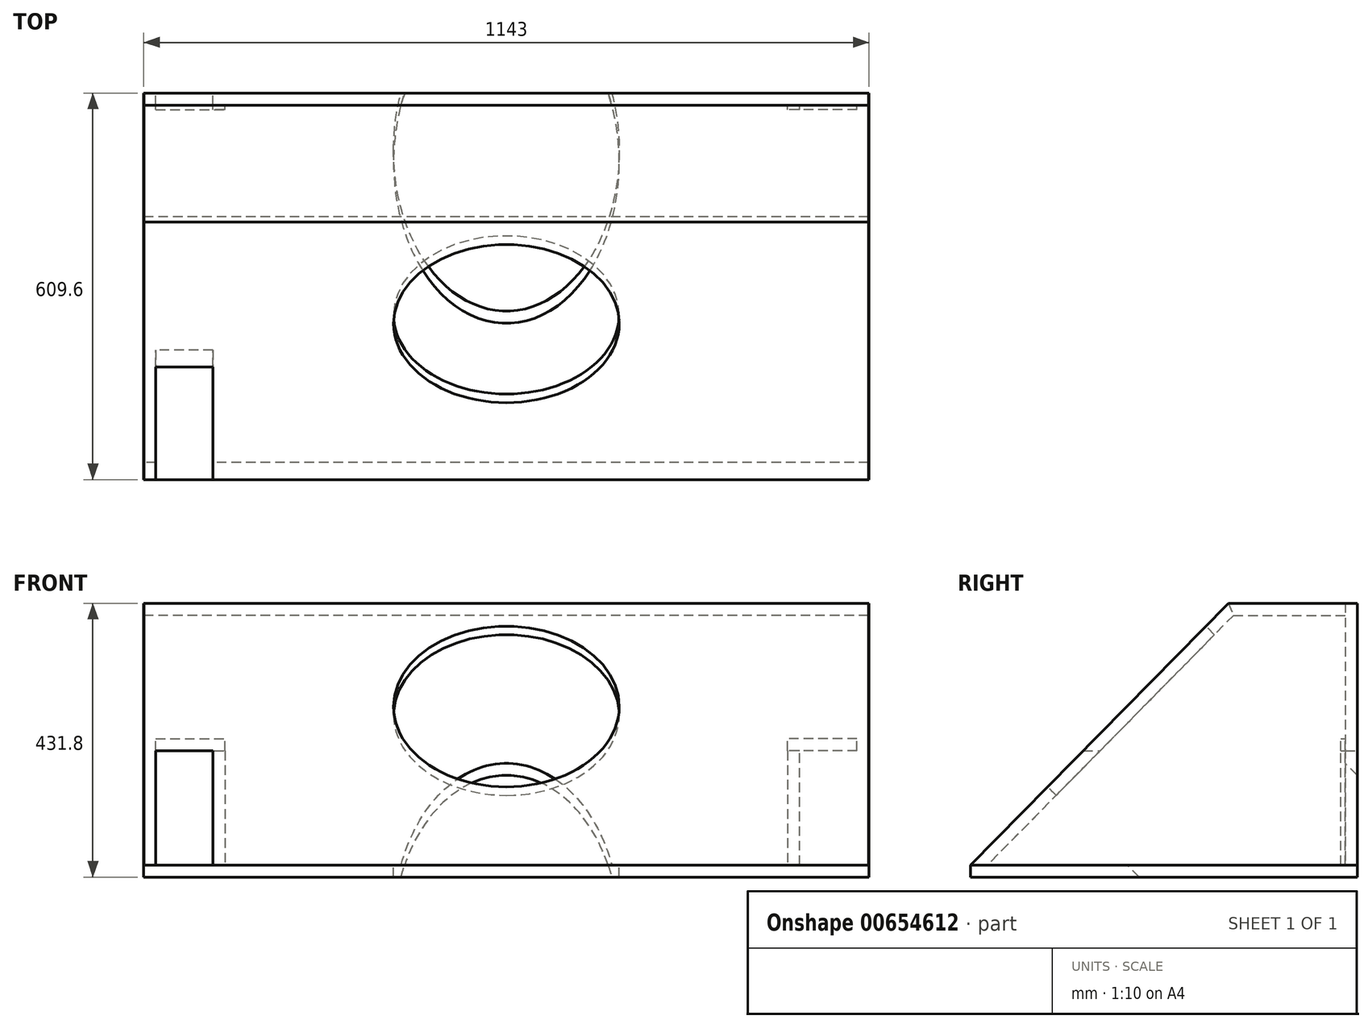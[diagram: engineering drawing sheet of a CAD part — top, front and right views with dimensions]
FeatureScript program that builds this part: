
annotation { "Feature Type Name" : "Feature", "Feature Type Description" : "" }
export const myFeature = defineFeature(function(context is Context, id is Id, definition is map)
    precondition{}
    {
        {
            assignVariable(context, id + "F0", {"name" : "Thickness", "anyValue" : 0.75});
        }
        {
            var Q0;
            Q0=qCreatedBy(makeId("Top.planeOp"),FACE);
            var sketch = newSketch(context, id + "F1", { "sketchPlane" : qUnion([Q0])});
            skLineSegment(sketch, "E0.bottom", {"start": v(571.5, 304.8) * mm, "end": v(-571.5, 304.8) * mm});
            skLineSegment(sketch, "E0.top", {"start": v(571.5, -304.8) * mm, "end": v(-571.5, -304.8) * mm});
            skLineSegment(sketch, "E0.left", {"start": v(571.5, 304.8) * mm, "end": v(571.5, -304.8) * mm});
            skLineSegment(sketch, "E0.right", {"start": v(-571.5, 304.8) * mm, "end": v(-571.5, -304.8) * mm});
            skPoint(sketch, "E0.middle", {"position": v(0, 0) * mm});
            skSolve(sketch);
        }
        {
            var Q0;
            Q0=qCreatedBy(makeId("Right.planeOp"),FACE);
            var Q1;
            Q1=sQuery(id+"F1.wireOp",VERTEX,"E0.left.end");
            cPlane(context, id + "F2", {"entities" : qUnion([Q0, Q1]), "cplaneType" : CPlaneType.PLANE_POINT, "offset" : 25.4 * mm, "width" : 152.4 * mm, "height" : 152.4 * mm});
        }
        {
            var Q0;
            Q0=qCreatedBy(id+"F2.planeOp",FACE);
            var sketch = newSketch(context, id + "F3", { "sketchPlane" : qUnion([Q0])});
            skLineSegment(sketch, "E1", {"start": v(-304.8, 0) * mm, "end": v(101.6, 412.75) * mm});
            skLineSegment(sketch, "E2", {"start": v(101.6, 412.75) * mm, "end": v(304.8, 412.75) * mm});
            skLineSegment(sketch, "E3", {"start": v(304.8, 412.75) * mm, "end": v(304.8, 0) * mm});
            skLineSegment(sketch, "E4", {"start": v(-304.8, 0) * mm, "end": v(304.8, 0) * mm});
            skSolve(sketch);
        }
        {
            var Q0;
            Q0=makeQuery(id+"F3.imprint","IMPRINT",FACE,{"disambiguationData":[TD([[makeQuery(id+"F3.imprint","IMPRINT",EDGE,{"derivedFrom":sQuery(id+"F3.wireOp",EDGE,"E1")}),-1.0]])]});
            extrude(context, id + "F4", {"entities" : qUnion([Q0]), "oppositeDirection" : true, "depth" : (getVariable(context, 'Thickness')) * mm, "offsetDistance" : 25.4 * mm});
        }
        {
            var Q0;
            Q0=qCreatedBy(id+"F2.planeOp",FACE);
            var sketch = newSketch(context, id + "F5", { "sketchPlane" : qUnion([Q0])});
            skLineSegment(sketch, "E5", {"start": v(304.8, 0) * mm, "end": v(-304.8, 0) * mm});
            skLineSegment(sketch, "E6", {"start": v(-304.8, -19.05) * mm, "end": v(-304.8, 0) * mm});
            skLineSegment(sketch, "E7", {"start": v(-304.8, -19.05) * mm, "end": v(304.8, -19.05) * mm});
            skLineSegment(sketch, "E8", {"start": v(304.8, -19.05) * mm, "end": v(304.8, 0) * mm});
            skSolve(sketch);
        }
        {
            var Q0;
            Q0=makeQuery(id+"F4.opExtrude","SWEPT_BODY",BODY,{"disambiguationData":[OSD([sQuery(id+"F3.wireOp",EDGE,"E1"),sQuery(id+"F3.wireOp",EDGE,"E2"),sQuery(id+"F3.wireOp",EDGE,"E3"),sQuery(id+"F3.wireOp",EDGE,"E4")])]});
            var Q1;
            Q1=qCreatedBy(makeId("Right.planeOp"),FACE);
            mirror(context, id + "F6", {"entities" : qUnion([Q0]), "mirrorPlane" : qUnion([Q1])});
        }
        {
            var Q0;
            Q0 = qSketchRegion(id + "F5", true);
            var Q1;
            Q1=makeQuery(id+"F6.opPattern","COPY",FACE,{"derivedFrom":makeQuery(id+"F4.opExtrude","CAP_FACE",FACE,{"disambiguationData":[OSD([sQuery(id+"F3.wireOp",EDGE,"E1"),sQuery(id+"F3.wireOp",EDGE,"E2"),sQuery(id+"F3.wireOp",EDGE,"E3"),sQuery(id+"F3.wireOp",EDGE,"E4")])],"isStart":true}),"instanceName":"1"});
            var Q2;
            Q2=makeQuery(id+"F6.opPattern","COPY",FACE,{"derivedFrom":makeQuery(id+"F4.opExtrude","CAP_FACE",FACE,{"disambiguationData":[OSD([sQuery(id+"F3.wireOp",EDGE,"E1"),sQuery(id+"F3.wireOp",EDGE,"E2"),sQuery(id+"F3.wireOp",EDGE,"E3"),sQuery(id+"F3.wireOp",EDGE,"E4")])],"isStart":false}),"instanceName":"1"});
            extrude(context, id + "F7", {"entities" : qUnion([Q0]), "endBound" : BoundingType.UP_TO_SURFACE, "oppositeDirection" : true, "depth" : 25.4 * mm, "endBoundEntityFace" : qUnion([Q1]), "offsetDistance" : 25.4 * mm});
        }
        {
            var Q0;
            Q0=qCreatedBy(makeId("Right.planeOp"),FACE);
            var sketch = newSketch(context, id + "F8", { "sketchPlane" : qUnion([Q0])});
            skLineSegment(sketch, "E9", {"start": v(-304.8, 0) * mm, "end": v(-278.07, 0) * mm});
            skLineSegment(sketch, "E10", {"start": v(-278.07, 0) * mm, "end": v(109.58, 393.7) * mm});
            skLineSegment(sketch, "E11", {"start": v(109.58, 393.7) * mm, "end": v(101.6, 412.75) * mm});
            skLineSegment(sketch, "E12", {"start": v(101.6, 412.75) * mm, "end": v(-304.8, 0) * mm});
            skSolve(sketch);
        }
        {
            var Q0;
            Q0 = qSketchRegion(id + "F8", true);
            var Q1;
            Q1=makeQuery(id+"F4.opExtrude","CAP_FACE",FACE,{"disambiguationData":[OSD([sQuery(id+"F3.wireOp",EDGE,"E1"),sQuery(id+"F3.wireOp",EDGE,"E2"),sQuery(id+"F3.wireOp",EDGE,"E3"),sQuery(id+"F3.wireOp",EDGE,"E4")])],"isStart":false});
            var Q2;
            Q2=makeQuery(id+"F6.opPattern","COPY",FACE,{"derivedFrom":makeQuery(id+"F4.opExtrude","CAP_FACE",FACE,{"disambiguationData":[OSD([sQuery(id+"F3.wireOp",EDGE,"E1"),sQuery(id+"F3.wireOp",EDGE,"E2"),sQuery(id+"F3.wireOp",EDGE,"E3"),sQuery(id+"F3.wireOp",EDGE,"E4")])],"isStart":false}),"instanceName":"1"});
            extrude(context, id + "F9", {"entities" : qUnion([Q0]), "endBound" : BoundingType.UP_TO_SURFACE, "depth" : 25.4 * mm, "endBoundEntityFace" : qUnion([Q1]), "offsetDistance" : 25.4 * mm, "hasSecondDirection" : true, "secondDirectionBound" : SecondDirectionBoundingType.UP_TO_SURFACE, "secondDirectionOppositeDirection" : true, "secondDirectionDepth" : 25.4 * mm, "secondDirectionBoundEntityFace" : qUnion([Q2])});
        }
        {
            var Q0;
            Q0=qCreatedBy(makeId("Right.planeOp"),FACE);
            var sketch = newSketch(context, id + "F10", { "sketchPlane" : qUnion([Q0])});
            skLineSegment(sketch, "E13", {"start": v(285.75, 412.75) * mm, "end": v(285.75, 0) * mm});
            skLineSegment(sketch, "E14", {"start": v(285.75, 412.75) * mm, "end": v(304.8, 412.75) * mm});
            skLineSegment(sketch, "E15", {"start": v(304.8, 0) * mm, "end": v(304.8, 412.75) * mm});
            skLineSegment(sketch, "E16", {"start": v(304.8, 0) * mm, "end": v(285.75, 0) * mm});
            skSolve(sketch);
        }
        {
            var Q0;
            Q0 = qSketchRegion(id + "F10", true);
            var Q1;
            Q1=makeQuery(id+"F4.opExtrude","CAP_FACE",FACE,{"disambiguationData":[OSD([sQuery(id+"F3.wireOp",EDGE,"E1"),sQuery(id+"F3.wireOp",EDGE,"E2"),sQuery(id+"F3.wireOp",EDGE,"E3"),sQuery(id+"F3.wireOp",EDGE,"E4")])],"isStart":false});
            var Q2;
            Q2=makeQuery(id+"F6.opPattern","COPY",FACE,{"derivedFrom":makeQuery(id+"F4.opExtrude","CAP_FACE",FACE,{"disambiguationData":[OSD([sQuery(id+"F3.wireOp",EDGE,"E1"),sQuery(id+"F3.wireOp",EDGE,"E2"),sQuery(id+"F3.wireOp",EDGE,"E3"),sQuery(id+"F3.wireOp",EDGE,"E4")])],"isStart":false}),"instanceName":"1"});
            extrude(context, id + "F11", {"entities" : qUnion([Q0]), "endBound" : BoundingType.UP_TO_SURFACE, "depth" : 25.4 * mm, "endBoundEntityFace" : qUnion([Q1]), "offsetDistance" : 25.4 * mm, "hasSecondDirection" : true, "secondDirectionBound" : SecondDirectionBoundingType.UP_TO_SURFACE, "secondDirectionOppositeDirection" : true, "secondDirectionDepth" : 25.4 * mm, "secondDirectionBoundEntityFace" : qUnion([Q2])});
        }
        {
            var Q0;
            Q0=makeQuery(id+"F6.opPattern","COPY",FACE,{"derivedFrom":makeQuery(id+"F4.opExtrude","CAP_FACE",FACE,{"disambiguationData":[OSD([sQuery(id+"F3.wireOp",EDGE,"E1"),sQuery(id+"F3.wireOp",EDGE,"E2"),sQuery(id+"F3.wireOp",EDGE,"E3"),sQuery(id+"F3.wireOp",EDGE,"E4")])],"isStart":false}),"instanceName":"1"});
            var sketch = newSketch(context, id + "F12", { "sketchPlane" : qUnion([Q0])});
            skLineSegment(sketch, "E17.bottom", {"start": v(101.6, 412.75) * mm, "end": v(285.75, 412.75) * mm});
            skLineSegment(sketch, "E17.top", {"start": v(109.58, 393.7) * mm, "end": v(285.75, 393.7) * mm});
            skLineSegment(sketch, "E17.left", {"start": v(101.6, 412.75) * mm, "end": v(109.58, 393.7) * mm});
            skLineSegment(sketch, "E17.right", {"start": v(285.75, 412.75) * mm, "end": v(285.75, 393.7) * mm});
            skSolve(sketch);
        }
        {
            var Q0;
            Q0 = qSketchRegion(id + "F12", true);
            var Q1;
            Q1=makeQuery(id+"F11.opExtrude","CAP_FACE",FACE,{"disambiguationData":[OSD([sQuery(id+"F10.wireOp",EDGE,"E13"),sQuery(id+"F10.wireOp",EDGE,"E14"),sQuery(id+"F10.wireOp",EDGE,"E15"),sQuery(id+"F10.wireOp",EDGE,"E16")])],"isStart":false});
            extrude(context, id + "F13", {"entities" : qUnion([Q0]), "endBound" : BoundingType.UP_TO_SURFACE, "depth" : 25.4 * mm, "endBoundEntityFace" : qUnion([Q1]), "offsetDistance" : 25.4 * mm});
        }
        {
            var Q0;
            Q0=makeQuery(id+"F9.opExtrude","SWEPT_FACE",FACE,{"disambiguationData":[OSD([sQuery(id+"F8.wireOp",EDGE,"E12")])]});
            var sketch = newSketch(context, id + "F14", { "sketchPlane" : qUnion([Q0])});
            skCircle(sketch, "E18", {"center": v(0, 136.8) * mm, "radius": 177.8 * mm});
            skSolve(sketch);
        }
        {
            var Q0;
            Q0 = qSketchRegion(id + "F14", true);
            extrude(context, id + "F15", {"entities" : qUnion([Q0]), "operationType" : NewBodyOperationType.REMOVE, "endBound" : BoundingType.THROUGH_ALL, "oppositeDirection" : true, "depth" : 25.4 * mm, "offsetDistance" : 25.4 * mm});
        }
        {
            var Q0;
            Q0=makeQuery(id+"F11.opExtrude","SWEPT_FACE",FACE,{"disambiguationData":[OSD([sQuery(id+"F10.wireOp",EDGE,"E15")])]});
            var sketch = newSketch(context, id + "F16", { "sketchPlane" : qUnion([Q0])});
            skLineSegment(sketch, "E19.bottom", {"start": v(552.45, 0) * mm, "end": v(462.4, 0) * mm});
            skLineSegment(sketch, "E19.top", {"start": v(552.45, 180.09) * mm, "end": v(462.4, 180.09) * mm});
            skLineSegment(sketch, "E19.left", {"start": v(552.45, 0) * mm, "end": v(552.45, 180.09) * mm});
            skLineSegment(sketch, "E19.right", {"start": v(462.4, 0) * mm, "end": v(462.4, 180.09) * mm});
            skSolve(sketch);
        }
        {
            var Q0;
            Q0 = qSketchRegion(id + "F16", true);
            extrude(context, id + "F17", {"entities" : qUnion([Q0]), "operationType" : NewBodyOperationType.REMOVE, "endBound" : BoundingType.THROUGH_ALL, "oppositeDirection" : true, "depth" : 25.4 * mm, "offsetDistance" : 25.4 * mm});
        }
        {
            var Q0;
            Q0=makeQuery(id+"F11.opExtrude","SWEPT_FACE",FACE,{"disambiguationData":[OSD([sQuery(id+"F10.wireOp",EDGE,"E13")])]});
            var sketch = newSketch(context, id + "F18", { "sketchPlane" : qUnion([Q0])});
            skLineSegment(sketch, "E20.bottom", {"start": v(-552.45, 180.09) * mm, "end": v(-443.36, 180.09) * mm});
            skLineSegment(sketch, "E20.top", {"start": v(-552.45, 199.14) * mm, "end": v(-443.36, 199.14) * mm});
            skLineSegment(sketch, "E20.left", {"start": v(-552.45, 180.09) * mm, "end": v(-552.45, 199.14) * mm});
            skLineSegment(sketch, "E20.right", {"start": v(-443.36, 180.09) * mm, "end": v(-443.36, 199.14) * mm});
            skLineSegment(sketch, "E21", {"start": v(-443.36, 189.61) * mm, "end": v(-462.4, 189.61) * mm, "construction": true});
            skSolve(sketch);
        }
        {
            var Q0;
            Q0 = qSketchRegion(id + "F18", true);
            extrude(context, id + "F19", {"entities" : qUnion([Q0]), "depth" : (7.8 - getVariable(context, 'Thickness')) * mm, "offsetDistance" : 25.4 * mm});
        }
        {
            var Q0;
            Q0=makeQuery(id+"F11.opExtrude","SWEPT_FACE",FACE,{"disambiguationData":[OSD([sQuery(id+"F10.wireOp",EDGE,"E13")])]});
            var sketch = newSketch(context, id + "F20", { "sketchPlane" : qUnion([Q0])});
            skLineSegment(sketch, "E22.bottom", {"start": v(-462.4, 180.09) * mm, "end": v(-443.36, 180.09) * mm});
            skLineSegment(sketch, "E22.top", {"start": v(-462.4, 0) * mm, "end": v(-443.36, 0) * mm});
            skLineSegment(sketch, "E22.left", {"start": v(-462.4, 180.09) * mm, "end": v(-462.4, 0) * mm});
            skLineSegment(sketch, "E22.right", {"start": v(-443.36, 180.09) * mm, "end": v(-443.36, 0) * mm});
            skSolve(sketch);
        }
        {
            var Q0;
            Q0 = qSketchRegion(id + "F20", true);
            var Q1;
            Q1=makeQuery(id+"F19.opExtrude","CAP_FACE",FACE,{"disambiguationData":[OSD([sQuery(id+"F18.wireOp",EDGE,"E20.bottom"),sQuery(id+"F18.wireOp",EDGE,"E20.top"),sQuery(id+"F18.wireOp",EDGE,"E20.left"),sQuery(id+"F18.wireOp",EDGE,"E20.right")])],"isStart":false});
            extrude(context, id + "F21", {"entities" : qUnion([Q0]), "endBound" : BoundingType.UP_TO_SURFACE, "depth" : 25.4 * mm, "endBoundEntityFace" : qUnion([Q1]), "offsetDistance" : 25.4 * mm});
        }
        {
            var Q0;
            Q0=makeQuery(id+"F19.opExtrude","SWEPT_BODY",BODY,{"disambiguationData":[OSD([sQuery(id+"F18.wireOp",EDGE,"E20.bottom"),sQuery(id+"F18.wireOp",EDGE,"E20.top"),sQuery(id+"F18.wireOp",EDGE,"E20.left"),sQuery(id+"F18.wireOp",EDGE,"E20.right")])]});
            var Q1;
            Q1=makeQuery(id+"F21.opExtrude","SWEPT_BODY",BODY,{"disambiguationData":[OSD([sQuery(id+"F20.wireOp",EDGE,"E22.bottom"),sQuery(id+"F20.wireOp",EDGE,"E22.top"),sQuery(id+"F20.wireOp",EDGE,"E22.left"),sQuery(id+"F20.wireOp",EDGE,"E22.right")])]});
            var Q2;
            Q2=qCreatedBy(makeId("Right.planeOp"),FACE);
            mirror(context, id + "F22", {"entities" : qUnion([Q0, Q1]), "mirrorPlane" : qUnion([Q2])});
        }
    });
